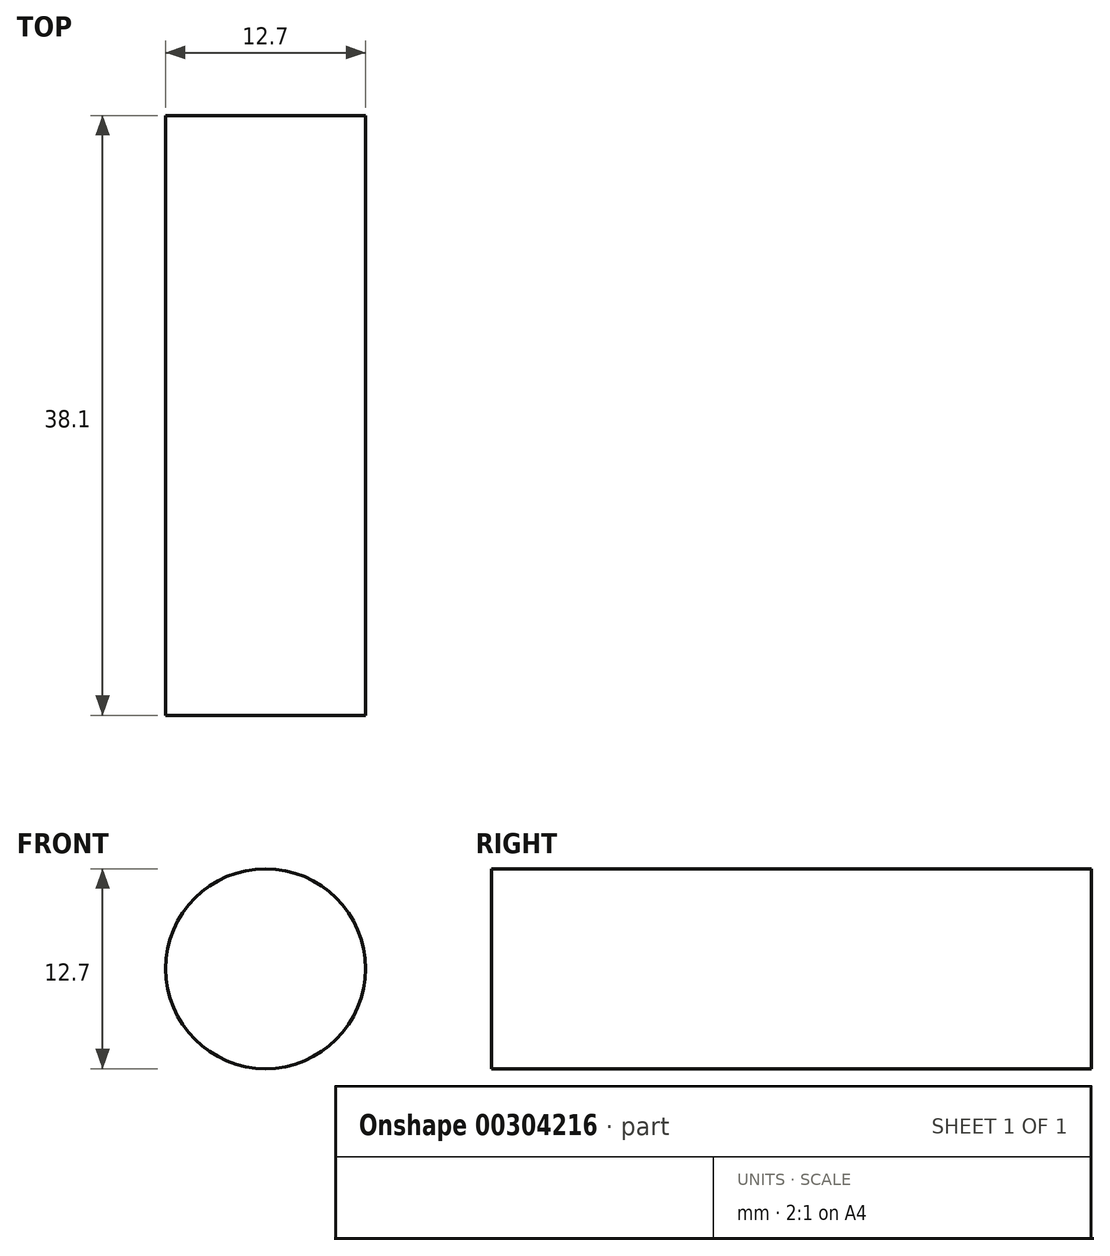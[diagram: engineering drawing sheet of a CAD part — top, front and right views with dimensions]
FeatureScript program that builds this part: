
annotation { "Feature Type Name" : "Feature", "Feature Type Description" : "" }
export const myFeature = defineFeature(function(context is Context, id is Id, definition is map)
    precondition{}
    {
        {
            var Q0;
            Q0=qCreatedBy(makeId("Front.planeOp"),FACE);
            var sketch = newSketch(context, id + "F0", { "sketchPlane" : qUnion([Q0])});
            skCircle(sketch, "E0", {"center": v(0, 0) * mm, "radius": 6.35 * mm});
            skSolve(sketch);
        }
        {
            var Q0;
            Q0 = qSketchRegion(id + "F0", true);
            extrude(context, id + "F1", {"entities" : qUnion([Q0]), "endBound" : BoundingType.SYMMETRIC, "depth" : 38.1 * mm});
        }
    });
